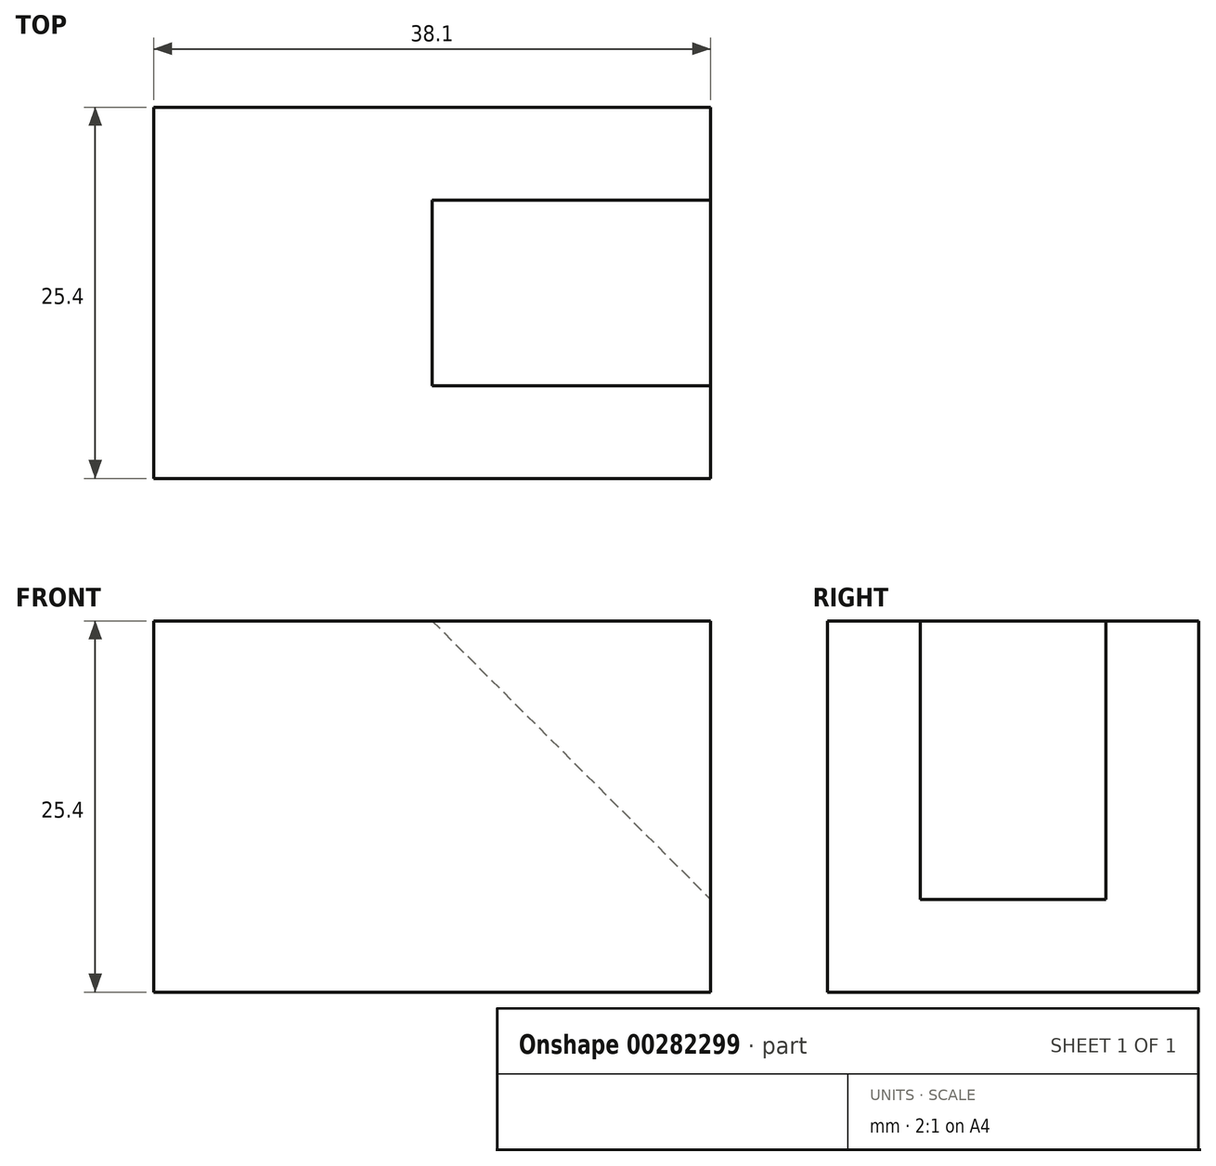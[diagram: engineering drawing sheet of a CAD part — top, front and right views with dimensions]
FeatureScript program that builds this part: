
annotation { "Feature Type Name" : "Feature", "Feature Type Description" : "" }
export const myFeature = defineFeature(function(context is Context, id is Id, definition is map)
    precondition{}
    {
        {
            var Q0;
            Q0=qCreatedBy(makeId("Top.planeOp"),FACE);
            var sketch = newSketch(context, id + "F0", { "sketchPlane" : qUnion([Q0])});
            skLineSegment(sketch, "E0.bottom", {"start": v(0, -12.7) * mm, "end": v(38.1, -12.7) * mm});
            skLineSegment(sketch, "E0.top", {"start": v(0, 12.7) * mm, "end": v(38.1, 12.7) * mm});
            skLineSegment(sketch, "E0.left", {"start": v(0, -12.7) * mm, "end": v(0, 12.7) * mm});
            skLineSegment(sketch, "E0.right", {"start": v(38.1, -12.7) * mm, "end": v(38.1, 12.7) * mm});
            skSolve(sketch);
        }
        {
            var Q0;
            Q0 = qSketchRegion(id + "F0", true);
            var Q1;
            Q1 = qSketchRegion(id + "F2", true);
            extrude(context, id + "F1", {"entities" : qUnion([Q0, Q1]), "endBound" : BoundingType.SYMMETRIC, "depth" : 25.4 * mm});
        }
        {
            var Q0;
            Q0=qCreatedBy(makeId("Front.planeOp"),FACE);
            var sketch = newSketch(context, id + "F2", { "sketchPlane" : qUnion([Q0])});
            skLineSegment(sketch, "E1", {"start": v(38.1, 12.7) * mm, "end": v(19.05, 12.7) * mm});
            skLineSegment(sketch, "E2", {"start": v(19.05, 12.7) * mm, "end": v(38.1, -6.35) * mm});
            skLineSegment(sketch, "E3", {"start": v(38.1, -6.35) * mm, "end": v(38.1, 12.7) * mm});
            skSolve(sketch);
        }
        {
            var Q0;
            Q0 = qSketchRegion(id + "F2", true);
            extrude(context, id + "F3", {"entities" : qUnion([Q0]), "operationType" : NewBodyOperationType.REMOVE, "endBound" : BoundingType.SYMMETRIC, "oppositeDirection" : true, "depth" : 12.7 * mm});
        }
    });
